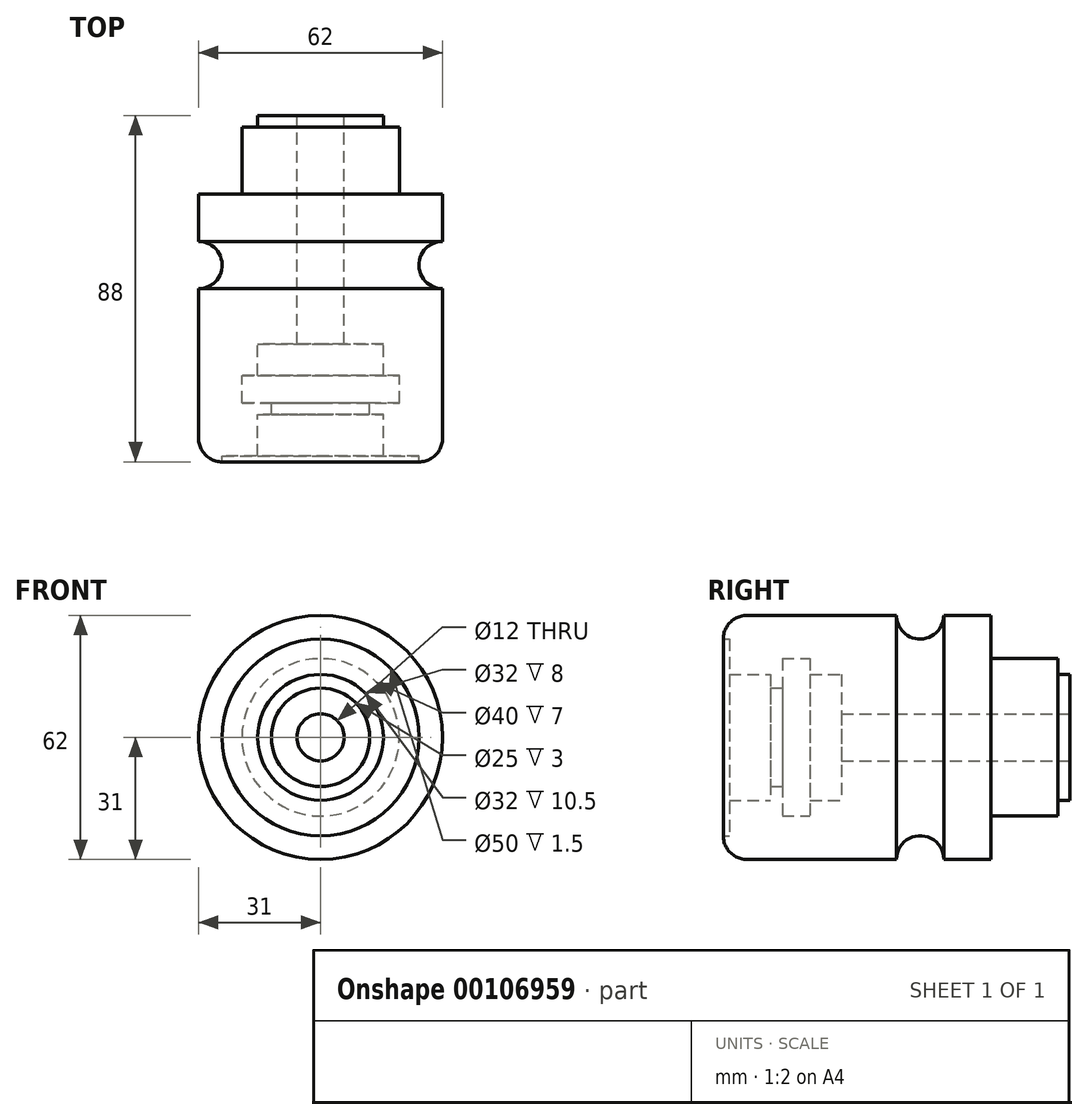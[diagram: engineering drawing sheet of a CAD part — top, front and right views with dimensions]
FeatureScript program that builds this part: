
annotation { "Feature Type Name" : "Feature", "Feature Type Description" : "" }
export const myFeature = defineFeature(function(context is Context, id is Id, definition is map)
    precondition{}
    {
        {
            var Q0;
            Q0=qCreatedBy(makeId("Right.planeOp"),FACE);
            var sketch = newSketch(context, id + "F0", { "sketchPlane" : qUnion([Q0])});
            skLineSegment(sketch, "E0", {"start": v(0, 0) * mm, "end": v(0, 16) * mm});
            skLineSegment(sketch, "E1", {"start": v(0, 16) * mm, "end": v(-3, 16) * mm});
            skLineSegment(sketch, "E2", {"start": v(-3, 16) * mm, "end": v(-3, 20) * mm});
            skLineSegment(sketch, "E3", {"start": v(-3, 20) * mm, "end": v(-20, 20) * mm});
            skLineSegment(sketch, "E4", {"start": v(-20, 20) * mm, "end": v(-20, 31) * mm});
            skLineSegment(sketch, "E5", {"start": v(-20, 31) * mm, "end": v(-32, 31) * mm});
            skArc(sketch, "E6", {"start": v(-44, 31) * mm, "mid": v(-38, 25) * mm, "end": v(-32, 31) * mm});
            skLineSegment(sketch, "E7", {"start": v(-44, 31) * mm, "end": v(-82, 31) * mm});
            skLineSegment(sketch, "E8", {"start": v(-88, 25) * mm, "end": v(-88, 0) * mm});
            skLineSegment(sketch, "E9", {"start": v(-88, 0) * mm, "end": v(0, 0) * mm});
            skPoint(sketch, "E10.visualSharp", {"position": v(-88, 31) * mm});
            skArc(sketch, "E10.filletArc", {"start": v(-82, 31) * mm, "mid": v(-86.24, 29.24) * mm, "end": v(-88, 25) * mm});
            skSolve(sketch);
        }
        {
            var Q0;
            Q0=qCreatedBy(makeId("Right.planeOp"),FACE);
            var sketch = newSketch(context, id + "F1", { "sketchPlane" : qUnion([Q0])});
            skLineSegment(sketch, "E11", {"start": v(0, 0) * mm, "end": v(-110.94, 0) * mm, "construction": true});
            skLineSegment(sketch, "E12", {"start": v(-88, 0) * mm, "end": v(-88, 62.07) * mm, "construction": true});
            skLineSegment(sketch, "E13.bottom", {"start": v(-88, 0) * mm, "end": v(-86.5, 0) * mm});
            skLineSegment(sketch, "E13.top", {"start": v(-88, 25) * mm, "end": v(-86.5, 25) * mm});
            skLineSegment(sketch, "E13.left", {"start": v(-88, 0) * mm, "end": v(-88, 25) * mm});
            skLineSegment(sketch, "E13.right", {"start": v(-86.5, 0) * mm, "end": v(-86.5, 25) * mm});
            skLineSegment(sketch, "E14.bottom", {"start": v(-86.5, 16) * mm, "end": v(-76, 16) * mm});
            skLineSegment(sketch, "E14.top", {"start": v(-86.5, 0) * mm, "end": v(-76, 0) * mm});
            skLineSegment(sketch, "E14.left", {"start": v(-86.5, 16) * mm, "end": v(-86.5, 0) * mm});
            skLineSegment(sketch, "E14.right", {"start": v(-76, 16) * mm, "end": v(-76, 0) * mm});
            skLineSegment(sketch, "E15.bottom", {"start": v(-76, 12.5) * mm, "end": v(-73, 12.5) * mm});
            skLineSegment(sketch, "E15.top", {"start": v(-76, 0) * mm, "end": v(-73, 0) * mm});
            skLineSegment(sketch, "E15.left", {"start": v(-76, 12.5) * mm, "end": v(-76, 0) * mm});
            skLineSegment(sketch, "E15.right", {"start": v(-73, 12.5) * mm, "end": v(-73, 0) * mm});
            skLineSegment(sketch, "E16.bottom", {"start": v(-73, 20) * mm, "end": v(-66, 20) * mm});
            skLineSegment(sketch, "E16.top", {"start": v(-73, 0) * mm, "end": v(-66, 0) * mm});
            skLineSegment(sketch, "E16.left", {"start": v(-73, 20) * mm, "end": v(-73, 0) * mm});
            skLineSegment(sketch, "E16.right", {"start": v(-66, 20) * mm, "end": v(-66, 0) * mm});
            skLineSegment(sketch, "E17.bottom", {"start": v(-66, 16) * mm, "end": v(-58, 16) * mm});
            skLineSegment(sketch, "E17.top", {"start": v(-66, 0) * mm, "end": v(-58, 0) * mm});
            skLineSegment(sketch, "E17.left", {"start": v(-66, 16) * mm, "end": v(-66, 0) * mm});
            skLineSegment(sketch, "E17.right", {"start": v(-58, 16) * mm, "end": v(-58, 0) * mm});
            skLineSegment(sketch, "E18.top", {"start": v(-58, 0) * mm, "end": v(0, 0) * mm});
            skLineSegment(sketch, "E18.left", {"start": v(-58, 6) * mm, "end": v(-58, 0) * mm});
            skLineSegment(sketch, "E19", {"start": v(0, 0) * mm, "end": v(0, 6) * mm});
            skLineSegment(sketch, "E20", {"start": v(0, 6) * mm, "end": v(-58, 6) * mm});
            skSolve(sketch);
        }
        {
            var Q0;
            Q0 = qSketchRegion(id + "F0", true);
            var Q1;
            Q1=sQuery(id+"F0.wireOp",EDGE,"E9");
            revolve(context, id + "F2", {"entities" : qUnion([Q0]), "axis" : qUnion([Q1]), "revolveType" : RevolveType.FULL});
        }
        {
            var Q0;
            Q0 = qSketchRegion(id + "F1", true);
            var Q1;
            Q1=sQuery(id+"F0.wireOp",EDGE,"E9");
            revolve(context, id + "F3", {"operationType" : NewBodyOperationType.REMOVE, "entities" : qUnion([Q0]), "axis" : qUnion([Q1]), "revolveType" : RevolveType.FULL, "oppositeDirection" : true});
        }
    });
